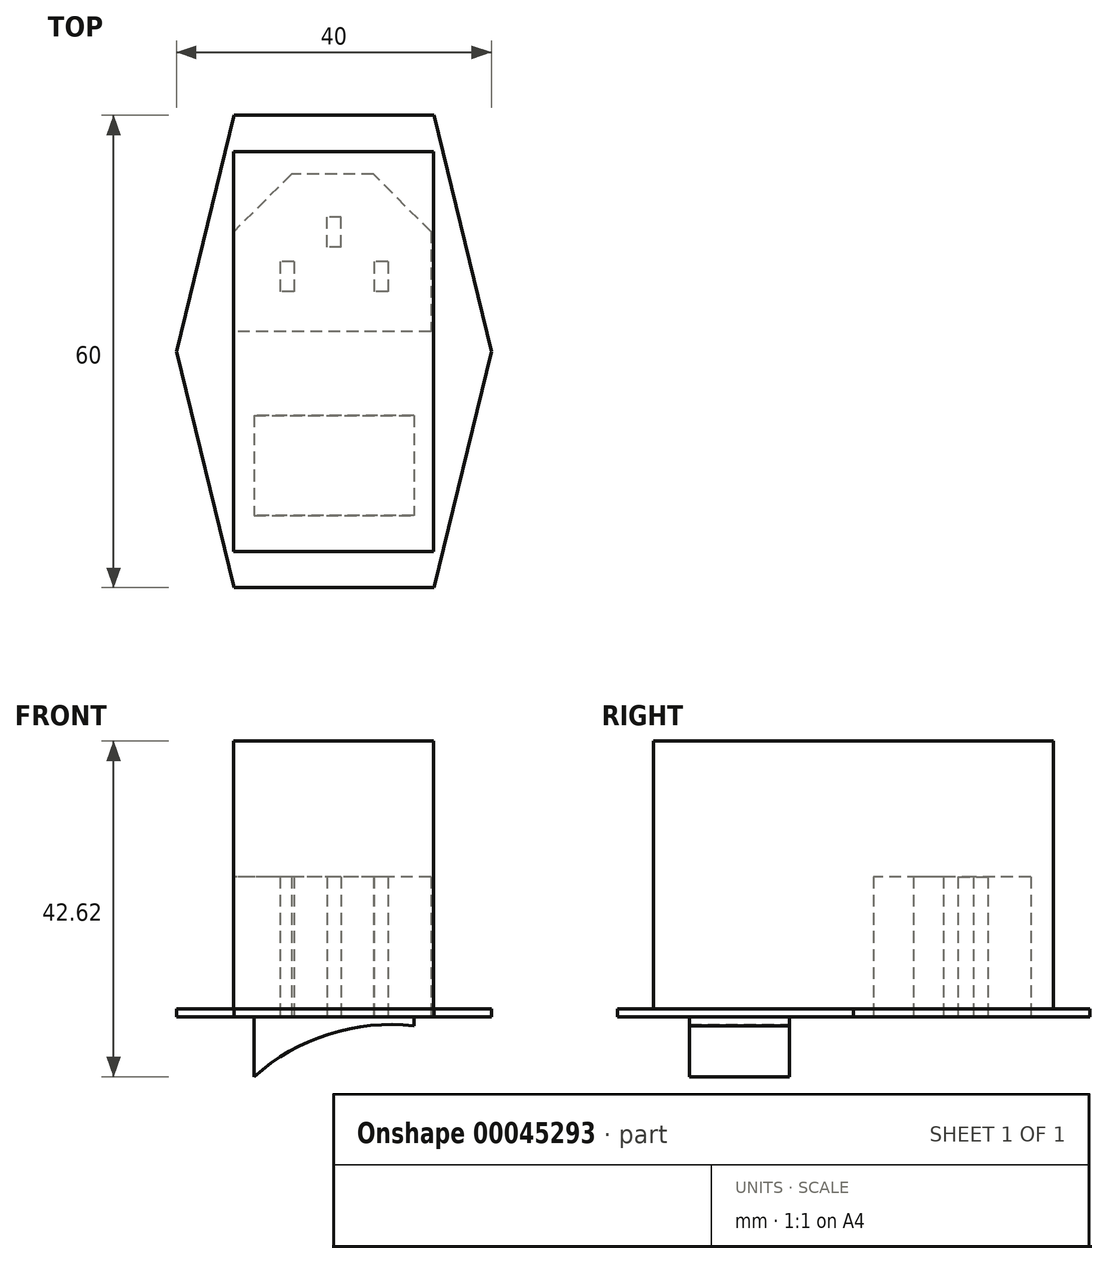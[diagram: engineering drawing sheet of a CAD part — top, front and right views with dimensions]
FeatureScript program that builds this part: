
annotation { "Feature Type Name" : "Feature", "Feature Type Description" : "" }
export const myFeature = defineFeature(function(context is Context, id is Id, definition is map)
    precondition{}
    {
        {
            var Q0;
            Q0=qCreatedBy(makeId("Top.planeOp"),FACE);
            var sketch = newSketch(context, id + "F0", { "sketchPlane" : qUnion([Q0])});
            skLineSegment(sketch, "E0", {"start": v(0, 30) * mm, "end": v(12.7, 30) * mm});
            skLineSegment(sketch, "E1", {"start": v(12.7, 30) * mm, "end": v(20, 0) * mm});
            skLineSegment(sketch, "E2", {"start": v(20, 0) * mm, "end": v(0, 0) * mm});
            skLineSegment(sketch, "E3", {"start": v(0, 0) * mm, "end": v(0, 30) * mm});
            skSolve(sketch);
        }
        {
            var Q0;
            Q0=makeQuery(id+"F0.imprint","IMPRINT",FACE,{"disambiguationData":[TD([[makeQuery(id+"F0.imprint","IMPRINT",EDGE,{"derivedFrom":sQuery(id+"F0.wireOp",EDGE,"E0")}),-1.0]])]});
            extrude(context, id + "F1", {"entities" : qUnion([Q0]), "depth" : 1 * mm});
        }
        {
            var Q0;
            Q0=makeQuery(id+"F1.opExtrude","SWEPT_BODY",BODY,{"disambiguationData":[OSD([sQuery(id+"F0.wireOp",EDGE,"E0"),sQuery(id+"F0.wireOp",EDGE,"E1"),sQuery(id+"F0.wireOp",EDGE,"E2"),sQuery(id+"F0.wireOp",EDGE,"E3")])]});
            var Q1;
            Q1=qCreatedBy(makeId("Front.planeOp"),FACE);
            mirror(context, id + "F2", {"operationType" : NewBodyOperationType.ADD, "entities" : qUnion([Q0]), "mirrorPlane" : qUnion([Q1])});
        }
        {
            var Q0;
            Q0=makeQuery(id+"F1.opExtrude","SWEPT_BODY",BODY,{"disambiguationData":[OSD([sQuery(id+"F0.wireOp",EDGE,"E0"),sQuery(id+"F0.wireOp",EDGE,"E1"),sQuery(id+"F0.wireOp",EDGE,"E2"),sQuery(id+"F0.wireOp",EDGE,"E3")])]});
            var Q1;
            Q1=qCreatedBy(makeId("Right.planeOp"),FACE);
            mirror(context, id + "F3", {"operationType" : NewBodyOperationType.ADD, "entities" : qUnion([Q0]), "mirrorPlane" : qUnion([Q1])});
        }
        {
            var Q0;
            {var subQ0=makeQuery(id+"F1.opExtrude","CAP_FACE",FACE,{"disambiguationData":[OSD([sQuery(id+"F0.wireOp",EDGE,"E0"),sQuery(id+"F0.wireOp",EDGE,"E1"),sQuery(id+"F0.wireOp",EDGE,"E2"),sQuery(id+"F0.wireOp",EDGE,"E3")])],"isStart":false});var subQ1=makeQuery(id+"F2.boolean.opBoolean","MERGE",FACE,{"derivedFrom":[subQ0,makeQuery(id+"F2.opPattern","COPY",FACE,{"derivedFrom":subQ0,"instanceName":"1"})]});Q0=makeQuery(id+"F3.boolean.opBoolean","MERGE",FACE,{"derivedFrom":[subQ1,makeQuery(id+"F3.opPattern","COPY",FACE,{"derivedFrom":subQ1,"instanceName":"1"})]});}
            var sketch = newSketch(context, id + "F4", { "sketchPlane" : qUnion([Q0])});
            skLineSegment(sketch, "E4.bottom", {"start": v(-12.75, 25.4) * mm, "end": v(12.65, 25.4) * mm});
            skLineSegment(sketch, "E4.top", {"start": v(-12.75, -25.4) * mm, "end": v(12.65, -25.4) * mm});
            skLineSegment(sketch, "E4.left", {"start": v(-12.75, 25.4) * mm, "end": v(-12.75, -25.4) * mm});
            skLineSegment(sketch, "E4.right", {"start": v(12.65, 25.4) * mm, "end": v(12.65, -25.4) * mm});
            skSolve(sketch);
        }
        {
            var Q0;
            Q0=makeQuery(id+"F4.imprint","IMPRINT",FACE,{"disambiguationData":[TD([[makeQuery(id+"F4.imprint","IMPRINT",EDGE,{"derivedFrom":sQuery(id+"F4.wireOp",EDGE,"E4.bottom")}),-1.0]])]});
            extrude(context, id + "F5", {"entities" : qUnion([Q0]), "operationType" : NewBodyOperationType.ADD, "depth" : 34 * mm});
        }
        {
            var Q0;
            {var subQ0=makeQuery(id+"F1.opExtrude","CAP_FACE",FACE,{"disambiguationData":[OSD([sQuery(id+"F0.wireOp",EDGE,"E0"),sQuery(id+"F0.wireOp",EDGE,"E1"),sQuery(id+"F0.wireOp",EDGE,"E2"),sQuery(id+"F0.wireOp",EDGE,"E3")])],"isStart":true});var subQ1=makeQuery(id+"F2.boolean.opBoolean","MERGE",FACE,{"derivedFrom":[subQ0,makeQuery(id+"F2.opPattern","COPY",FACE,{"derivedFrom":subQ0,"instanceName":"1"})]});Q0=makeQuery(id+"F3.boolean.opBoolean","MERGE",FACE,{"derivedFrom":[subQ1,makeQuery(id+"F3.opPattern","COPY",FACE,{"derivedFrom":subQ1,"instanceName":"1"})]});}
            var sketch = newSketch(context, id + "F6", { "sketchPlane" : qUnion([Q0])});
            skLineSegment(sketch, "E5.bottom", {"start": v(12.3, -22.54) * mm, "end": v(-12.7, -22.54) * mm});
            skLineSegment(sketch, "E5.top", {"start": v(12.3, -2.54) * mm, "end": v(-12.7, -2.54) * mm});
            skLineSegment(sketch, "E5.left", {"start": v(12.3, -22.54) * mm, "end": v(12.3, -2.54) * mm});
            skLineSegment(sketch, "E5.right", {"start": v(-12.7, -22.54) * mm, "end": v(-12.7, -2.54) * mm});
            skLineSegment(sketch, "E6", {"start": v(-5.4, -22.54) * mm, "end": v(-12.7, -15.24) * mm});
            skLineSegment(sketch, "E7", {"start": v(12.3, -15.24) * mm, "end": v(5, -22.54) * mm});
            skLineSegment(sketch, "E8.bottom", {"start": v(6.86, -11.41) * mm, "end": v(5.08, -11.41) * mm});
            skLineSegment(sketch, "E8.top", {"start": v(6.86, -7.6) * mm, "end": v(5.08, -7.6) * mm});
            skLineSegment(sketch, "E8.left", {"start": v(6.86, -11.41) * mm, "end": v(6.86, -7.6) * mm});
            skLineSegment(sketch, "E8.right", {"start": v(5.08, -11.41) * mm, "end": v(5.08, -7.6) * mm});
            skLineSegment(sketch, "E9.bottom", {"start": v(-5.08, -11.41) * mm, "end": v(-6.86, -11.41) * mm});
            skLineSegment(sketch, "E9.top", {"start": v(-5.08, -7.6) * mm, "end": v(-6.86, -7.6) * mm});
            skLineSegment(sketch, "E9.left", {"start": v(-5.08, -11.41) * mm, "end": v(-5.08, -7.6) * mm});
            skLineSegment(sketch, "E9.right", {"start": v(-6.86, -11.41) * mm, "end": v(-6.86, -7.6) * mm});
            skLineSegment(sketch, "E10.bottom", {"start": v(0.93, -13.29) * mm, "end": v(-0.85, -13.29) * mm});
            skLineSegment(sketch, "E10.top", {"start": v(0.93, -17.1) * mm, "end": v(-0.85, -17.1) * mm});
            skLineSegment(sketch, "E10.left", {"start": v(0.93, -13.29) * mm, "end": v(0.93, -17.1) * mm});
            skLineSegment(sketch, "E10.right", {"start": v(-0.85, -13.29) * mm, "end": v(-0.85, -17.1) * mm});
            skSolve(sketch);
        }
        {
            var Q0;
            {var subQ2=sQuery(id+"F6.wireOp",EDGE,"E5.top");Q0=makeQuery(id+"F6.imprint","IMPRINT",FACE,{"disambiguationData":[TD([[makeQuery(id+"F6.imprint","IMPRINT",EDGE,{"derivedFrom":subQ2}),1.0]])]});}
            extrude(context, id + "F7", {"entities" : qUnion([Q0]), "operationType" : NewBodyOperationType.REMOVE, "oppositeDirection" : true, "depth" : 17.78 * mm});
        }
        {
            var Q0;
            {var subQ0=sQuery(id+"F0.wireOp",EDGE,"E0");var subQ1=sQuery(id+"F0.wireOp",EDGE,"E1");var subQ2=makeQuery(id+"F1.opExtrude","CAP_FACE",FACE,{"disambiguationData":[OSD([subQ0,subQ1,sQuery(id+"F0.wireOp",EDGE,"E2"),sQuery(id+"F0.wireOp",EDGE,"E3")])],"isStart":true});var subQ3=makeQuery(id+"F2.boolean.opBoolean","MERGE",FACE,{"derivedFrom":[subQ2,makeQuery(id+"F2.opPattern","COPY",FACE,{"derivedFrom":subQ2,"instanceName":"1"})]});var subQ6=makeQuery(id+"F1.opExtrude","SWEPT_FACE",FACE,{"disambiguationData":[OSD([subQ0])]});Q0=makeQuery(id+"F7.boolean.opBoolean","SPLIT",FACE,{"disambiguationData":[TD([subQ6])],"derivedFrom":makeQuery(id+"F3.boolean.opBoolean","MERGE",FACE,{"derivedFrom":[subQ3,makeQuery(id+"F3.opPattern","COPY",FACE,{"derivedFrom":subQ3,"instanceName":"1"})]})});}
            var sketch = newSketch(context, id + "F8", { "sketchPlane" : qUnion([Q0])});
            skLineSegment(sketch, "E11.bottom", {"start": v(10.16, 8.11) * mm, "end": v(-10.16, 8.11) * mm});
            skLineSegment(sketch, "E11.top", {"start": v(10.16, 20.81) * mm, "end": v(-10.16, 20.81) * mm});
            skLineSegment(sketch, "E11.left", {"start": v(10.16, 8.11) * mm, "end": v(10.16, 20.81) * mm});
            skLineSegment(sketch, "E11.right", {"start": v(-10.16, 8.11) * mm, "end": v(-10.16, 20.81) * mm});
            skSolve(sketch);
        }
        {
            var Q0;
            Q0=makeQuery(id+"F8.imprint","IMPRINT",FACE,{"disambiguationData":[TD([[makeQuery(id+"F8.imprint","IMPRINT",EDGE,{"derivedFrom":sQuery(id+"F8.wireOp",EDGE,"E11.bottom")}),-1.0]])]});
            extrude(context, id + "F9", {"entities" : qUnion([Q0]), "operationType" : NewBodyOperationType.ADD, "depth" : 7.62 * mm});
        }
        {
            var Q0;
            Q0=makeQuery(id+"F9.opExtrude","SWEPT_FACE",FACE,{"disambiguationData":[OSD([sQuery(id+"F8.wireOp",EDGE,"E11.bottom")])]});
            var sketch = newSketch(context, id + "F10", { "sketchPlane" : qUnion([Q0])});
            skLineSegment(sketch, "E12", {"start": v(-10.16, -1.17) * mm, "end": v(10.16, -7.62) * mm});
            skCircle(sketch, "E13", {"center": v(-7.23, -27.17) * mm, "radius": 26.17 * mm});
            skPoint(sketch, "E13.third.point", {"position": v(0.45, -2.16) * mm});
            skSolve(sketch);
        }
        {
            var Q0;
            {var subQ2=sQuery(id+"F10.wireOp",EDGE,"E12");Q0=makeQuery(id+"F10.imprint","IMPRINT",FACE,{"disambiguationData":[TD([[makeQuery(id+"F10.imprint","IMPRINT",EDGE,{"derivedFrom":subQ2}),-1.0]])]});}
            var Q1;
            {var subQ2=sQuery(id+"F10.wireOp",EDGE,"E12");Q1=makeQuery(id+"F10.imprint","IMPRINT",FACE,{"disambiguationData":[TD([[makeQuery(id+"F10.imprint","IMPRINT",EDGE,{"derivedFrom":subQ2}),1.0]])]});}
            extrude(context, id + "F11", {"entities" : qUnion([Q0, Q1]), "operationType" : NewBodyOperationType.REMOVE, "oppositeDirection" : true, "depth" : 25.4 * mm});
        }
    });
